# Revit family: Upper_Bottle_Filling_Station_Bi-Level_Pedestal_Elkay-LK4420BF1UDB_EVG_BLU_GRY_BLK
name_source: partatom
category: Plumbing Fixtures
units: mm (PartAtom-declared; Revit-internal decimal feet)

## family parameters
Always vertical = Yes
Cut with Voids When Loaded = No
Maintain Annotation Orientation = No
OmniClass Number = 23.65.70.14.11
OmniClass Title = Drinking Fountains/Coolers
Part Type = Normal
Room Calculation Point = No
Round Connector Dimension = Use Diameter
Shared = No
Work Plane-Based = No

## types (4) — shared parameters
ARM Height = 4.000"
Activation Method = Mechanical Button
Approx.Shipping Weight (lbs) = 205
Assembly Code = D2010.60
Base Thickness = 0.130"
Bottom Arm = 4.130"
Default Elevation = 0.000"
Description = Outdoor ezH2O® Upper Bottle Filling Station Bi-Level Pedestal with Pet Station Non-Filtered Non-Refrigerated
Height = 64.000"
Inlet Connection Size (inch) = 0.375"
Length = 26.000"
Manufacturer = Elkay Manufracturer Company
Manufacturer Brand = Elkay (by Zurn Elkay Water Solution)
Outlet connection Size (inch) = 1.500"
Product Documentation Link = https://www.elkayfiles.com
Product Installation Sheet URL = https://www.elkayfiles.com
Product Page URL = https://www.elkay.com
Product Weight (lbs) = 200
Product data URL = https://www.bimobject.com
Repair Parts URL = https://www.elkayfiles.com
Secoundary Material = Finish-Elkay-Stainless Steel
Trap Primer = Yes
URL = https://www.elkay.com
Width = 31.000"
zero-valued in all types: CWFU, HWFU, WFU

## per-type parameters (varying)
| type | Main Material | Model |
| LK4420BF1UDBLU ( Upper Bottle Filling Station Bi-Level Pedestal with Pet Station Non-Filtered Non-Refrigerated blue ) | Finish-Elkay-Blue | LK4420BF1UDBBLU |
| LK4420BF1UDBBLK ( Upper Bottle Filling Station Bi-Level Pedestal with Pet Station Non-Filtered Non-Refrigerated Black ) | Finish-Elkay-Black | LK4420BF1UDBBLK |
| LK4420BF1UDBEVG ( Upper Bottle Filling Station Bi-Level Pedestal with Pet Station Non-Filtered Non-Refrigerated Blue ) | Finish-Elkay-Blue | LK4420BF1UDBEVG |
| LK4420BF1UDBGRY ( Upper Bottle Filling Station Bi-Level Pedestal with Pet Station Non-Filtered Non-Refrigerated Gray ) | Finish-Elkay-Gray | LK4420BF1UDBGRY |

## geometry (parser evidence)
native form markers: Sweep x5
no freeform markers — native parametric forms only
